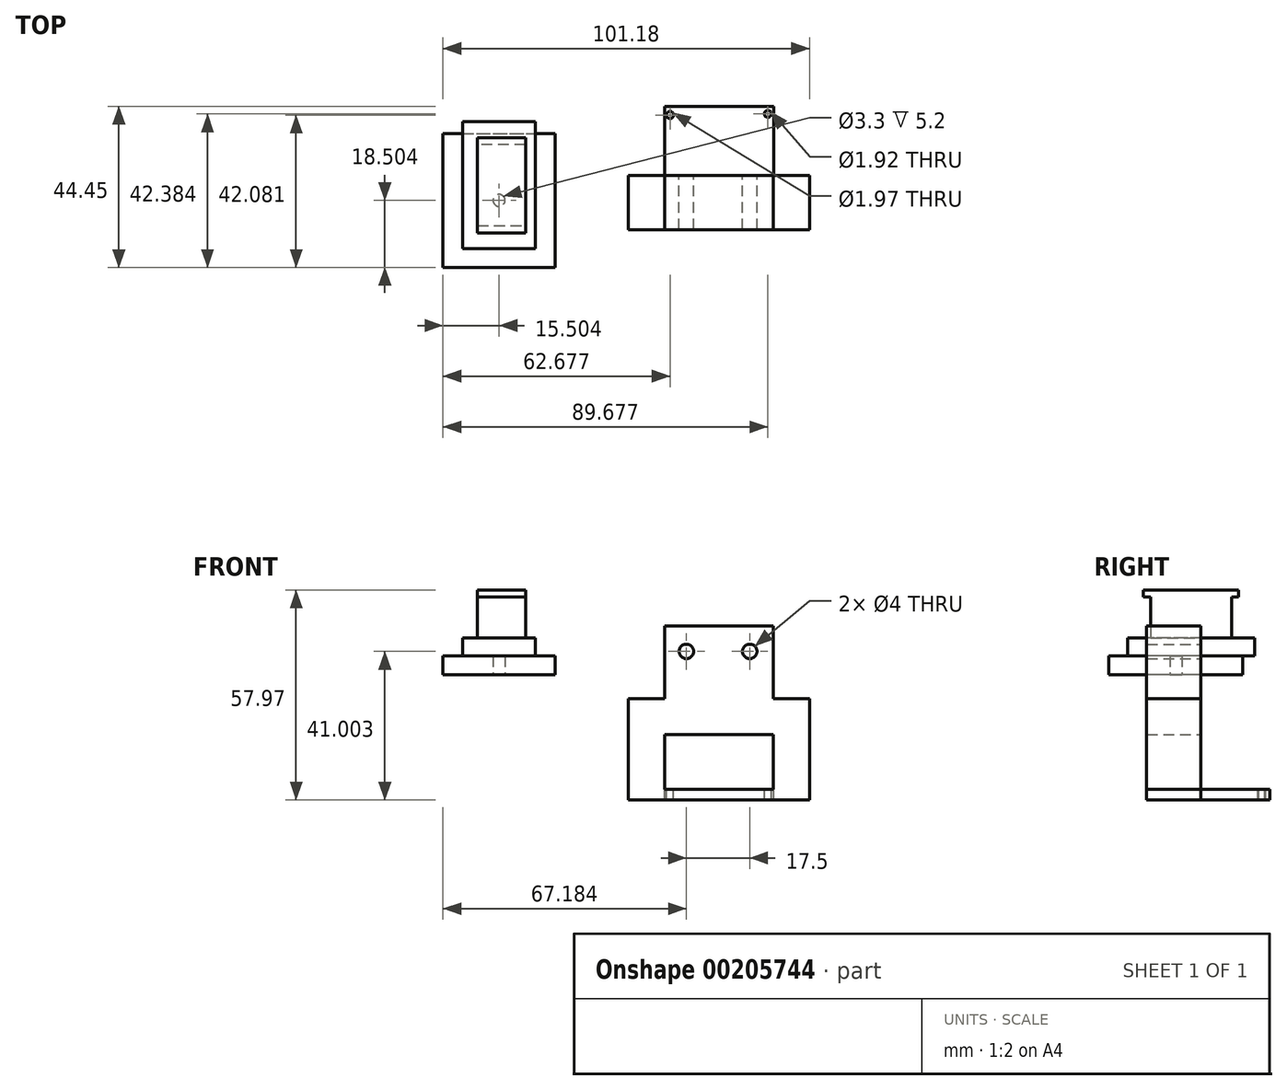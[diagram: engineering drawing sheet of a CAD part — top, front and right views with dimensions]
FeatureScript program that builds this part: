
annotation { "Feature Type Name" : "Feature", "Feature Type Description" : "" }
export const myFeature = defineFeature(function(context is Context, id is Id, definition is map)
    precondition{}
    {
        {
            var Q0;
            Q0=qCreatedBy(makeId("Front.planeOp"),FACE);
            var sketch = newSketch(context, id + "F0", { "sketchPlane" : qUnion([Q0])});
            skLineSegment(sketch, "E0.bottom", {"start": v(-18.33, 11.23) * mm, "end": v(11.67, 11.23) * mm});
            skLineSegment(sketch, "E0.top", {"start": v(-18.33, -18.77) * mm, "end": v(11.67, -18.77) * mm});
            skLineSegment(sketch, "E0.left", {"start": v(-18.33, 11.23) * mm, "end": v(-18.33, -18.77) * mm});
            skLineSegment(sketch, "E0.right", {"start": v(11.67, 11.23) * mm, "end": v(11.67, -18.77) * mm});
            skCircle(sketch, "E1", {"center": v(-12.33, 4.23) * mm, "radius": 2 * mm});
            skCircle(sketch, "E2", {"center": v(5.17, 4.23) * mm, "radius": 2 * mm});
            skPoint(sketch, "E3", {"position": v(-3.33, 11.23) * mm});
            skSolve(sketch);
        }
        {
            var Q0;
            Q0=makeQuery(id+"F0.imprint","IMPRINT",FACE,{"disambiguationData":[TD([[makeQuery(id+"F0.imprint","IMPRINT",EDGE,{"derivedFrom":sQuery(id+"F0.wireOp",EDGE,"E0.bottom")}),-1.0]])]});
            extrude(context, id + "F1", {"entities" : qUnion([Q0]), "depth" : 15 * mm});
        }
        {
            var Q0;
            Q0=makeQuery(id+"F1.opExtrude","SWEPT_FACE",FACE,{"disambiguationData":[OSD([sQuery(id+"F0.wireOp",EDGE,"E0.left")])]});
            var sketch = newSketch(context, id + "F2", { "sketchPlane" : qUnion([Q0])});
            skLineSegment(sketch, "E4.bottom", {"start": v(0, -8.77) * mm, "end": v(15, -8.77) * mm});
            skLineSegment(sketch, "E4.top", {"start": v(0, -33.77) * mm, "end": v(15, -33.77) * mm});
            skLineSegment(sketch, "E4.left", {"start": v(0, -8.77) * mm, "end": v(0, -33.77) * mm});
            skLineSegment(sketch, "E4.right", {"start": v(15, -8.77) * mm, "end": v(15, -33.77) * mm});
            skPoint(sketch, "E5", {"position": v(15, -3.77) * mm});
            skSolve(sketch);
        }
        {
            var Q0;
            Q0 = qSketchRegion(id + "F2", true);
            extrude(context, id + "F3", {"entities" : qUnion([Q0]), "operationType" : NewBodyOperationType.ADD, "depth" : 10 * mm});
        }
        {
            var Q0;
            Q0=makeQuery(id+"F1.opExtrude","SWEPT_FACE",FACE,{"disambiguationData":[OSD([sQuery(id+"F0.wireOp",EDGE,"E0.right")])]});
            var sketch = newSketch(context, id + "F4", { "sketchPlane" : qUnion([Q0])});
            skLineSegment(sketch, "E6.bottom", {"start": v(-15, -8.77) * mm, "end": v(0, -8.77) * mm});
            skLineSegment(sketch, "E6.top", {"start": v(-15, -33.77) * mm, "end": v(0, -33.77) * mm});
            skLineSegment(sketch, "E6.left", {"start": v(-15, -8.77) * mm, "end": v(-15, -33.77) * mm});
            skLineSegment(sketch, "E6.right", {"start": v(0, -8.77) * mm, "end": v(0, -33.77) * mm});
            skSolve(sketch);
        }
        {
            var Q0;
            Q0 = qSketchRegion(id + "F4", true);
            extrude(context, id + "F5", {"entities" : qUnion([Q0]), "operationType" : NewBodyOperationType.ADD, "depth" : 10 * mm});
        }
        {
            var Q0;
            Q0=makeQuery(id+"F3.opExtrude","SWEPT_FACE",FACE,{"disambiguationData":[OSD([sQuery(id+"F2.wireOp",EDGE,"E4.top")])]});
            var sketch = newSketch(context, id + "F6", { "sketchPlane" : qUnion([Q0])});
            skLineSegment(sketch, "E7.bottom", {"start": v(-28.33, 15) * mm, "end": v(21.65, 15) * mm});
            skLineSegment(sketch, "E7.top", {"start": v(-28.33, 0) * mm, "end": v(21.65, 0) * mm});
            skLineSegment(sketch, "E7.left", {"start": v(-28.33, 15) * mm, "end": v(-28.33, 0) * mm});
            skLineSegment(sketch, "E7.right", {"start": v(21.65, 15) * mm, "end": v(21.65, 0) * mm});
            skLineSegment(sketch, "E8.bottom", {"start": v(-18.33, 0) * mm, "end": v(11.76, 0) * mm});
            skLineSegment(sketch, "E8.top", {"start": v(-18.33, -19) * mm, "end": v(11.76, -19) * mm});
            skLineSegment(sketch, "E8.left", {"start": v(-18.33, 0) * mm, "end": v(-18.33, -19) * mm});
            skLineSegment(sketch, "E8.right", {"start": v(11.76, 0) * mm, "end": v(11.76, -19) * mm});
            skCircle(sketch, "E9", {"center": v(-16.83, -16.63) * mm, "radius": 0.99 * mm});
            skCircle(sketch, "E10", {"center": v(10.17, -16.93) * mm, "radius": 0.96 * mm});
            skSolve(sketch);
        }
        {
            var Q0;
            Q0 = qSketchRegion(id + "F6", true);
            extrude(context, id + "F7", {"entities" : qUnion([Q0]), "operationType" : NewBodyOperationType.ADD, "depth" : 3 * mm});
        }
        {
            var Q0;
            Q0=qCreatedBy(makeId("Top.planeOp"),FACE);
            var sketch = newSketch(context, id + "F8", { "sketchPlane" : qUnion([Q0])});
            skLineSegment(sketch, "E11.bottom", {"start": v(-79.5, 11.55) * mm, "end": v(-48.5, 11.55) * mm});
            skLineSegment(sketch, "E11.top", {"start": v(-79.5, -25.45) * mm, "end": v(-48.5, -25.45) * mm});
            skLineSegment(sketch, "E11.left", {"start": v(-79.5, 11.55) * mm, "end": v(-79.5, -25.45) * mm});
            skLineSegment(sketch, "E11.right", {"start": v(-48.5, 11.55) * mm, "end": v(-48.5, -25.45) * mm});
            skLineSegment(sketch, "E12", {"start": v(-64, 11.55) * mm, "end": v(-64, -25.45) * mm, "construction": true});
            skLineSegment(sketch, "E13", {"start": v(-79.5, -6.95) * mm, "end": v(-48.5, -6.95) * mm, "construction": true});
            skCircle(sketch, "E14", {"center": v(-64, -6.95) * mm, "radius": 1.65 * mm});
            skSolve(sketch);
        }
        {
            var Q0;
            Q0 = qSketchRegion(id + "F8", true);
            extrude(context, id + "F9", {"entities" : qUnion([Q0]), "depth" : 3 * mm});
        }
        {
            var Q0;
            Q0=makeQuery(id+"F9.opExtrude","CAP_FACE",FACE,{"disambiguationData":[OSD([sQuery(id+"F8.wireOp",EDGE,"E11.bottom"),sQuery(id+"F8.wireOp",EDGE,"E11.top"),sQuery(id+"F8.wireOp",EDGE,"E11.left"),sQuery(id+"F8.wireOp",EDGE,"E11.right"),sQuery(id+"F8.wireOp",EDGE,"IWCKZ5gG-MOeN-IYZW-2EvN-JKWWDjgxmHPc"),sQuery(id+"F8.wireOp",EDGE,"644afa14-c5a4-4717-896c-2b00ea7ac0db0.MirrorC"),sQuery(id+"F8.wireOp",EDGE,"57038aa0-a765-417c-a0be-fbad03bbe3f50.MirrorC"),sQuery(id+"F8.wireOp",EDGE,"708bdf5b-5082-4a79-8eaa-554b4d0072140.MirrorC")])],"isStart":false});
            var sketch = newSketch(context, id + "F10", { "sketchPlane" : qUnion([Q0])});
            skLineSegment(sketch, "E15.bottom", {"start": v(-74, 14.75) * mm, "end": v(-54, 14.75) * mm});
            skLineSegment(sketch, "E15.top", {"start": v(-74, -20.25) * mm, "end": v(-54, -20.25) * mm});
            skLineSegment(sketch, "E15.left", {"start": v(-74, 14.75) * mm, "end": v(-74, -20.25) * mm});
            skLineSegment(sketch, "E15.right", {"start": v(-54, 14.75) * mm, "end": v(-54, -20.25) * mm});
            skLineSegment(sketch, "E16.bottom", {"start": v(-70.01, 8.4) * mm, "end": v(-56.71, 8.4) * mm});
            skLineSegment(sketch, "E16.top", {"start": v(-70.01, -13.9) * mm, "end": v(-56.71, -13.9) * mm});
            skLineSegment(sketch, "E16.left", {"start": v(-70.01, 8.4) * mm, "end": v(-70.01, -13.9) * mm});
            skLineSegment(sketch, "E16.right", {"start": v(-56.71, 8.4) * mm, "end": v(-56.71, -13.9) * mm});
            skPoint(sketch, "E16.middle", {"position": v(-63.36, -2.75) * mm});
            skPoint(sketch, "E16.middle.positionSnap0", {"position": v(-54, -2.75) * mm});
            skPoint(sketch, "E16.centerSnap0", {"position": v(-54, -2.75) * mm});
            skPoint(sketch, "E17", {"position": v(-64, 14.75) * mm});
            skSolve(sketch);
        }
        {
            var Q0;
            Q0 = qSketchRegion(id + "F10", true);
            var Q1;
            Q1=makeQuery(id+"F10.imprint","IMPRINT",FACE,{"disambiguationData":[TD([[makeQuery(id+"F10.imprint","IMPRINT",EDGE,{"derivedFrom":sQuery(id+"F10.wireOp",EDGE,"E16.bottom")}),-1.0]])]});
            var Q2;
            Q2=makeQuery(id+"F10.imprint","IMPRINT",FACE,{"disambiguationData":[TD([[makeQuery(id+"F10.imprint","IMPRINT",EDGE,{"derivedFrom":makeQuery(id+"F9.opExtrude","CAP_EDGE",EDGE,{"disambiguationData":[OSD([sQuery(id+"F8.wireOp",EDGE,"E14")])],"isStart":false})}),1.0]])]});
            extrude(context, id + "F11", {"entities" : qUnion([Q0, Q1, Q2]), "operationType" : NewBodyOperationType.ADD, "depth" : 5 * mm});
        }
        {
            var Q0;
            Q0=makeQuery(id+"F10.imprint","IMPRINT",FACE,{"disambiguationData":[TD([[makeQuery(id+"F10.imprint","IMPRINT",EDGE,{"derivedFrom":sQuery(id+"F10.wireOp",EDGE,"E16.bottom")}),-1.0]])]});
            var Q1;
            Q1=makeQuery(id+"F10.imprint","IMPRINT",FACE,{"disambiguationData":[TD([[makeQuery(id+"F10.imprint","IMPRINT",EDGE,{"derivedFrom":makeQuery(id+"F9.opExtrude","CAP_EDGE",EDGE,{"disambiguationData":[OSD([sQuery(id+"F8.wireOp",EDGE,"E14")])],"isStart":false})}),1.0]])]});
            extrude(context, id + "F12", {"entities" : qUnion([Q0, Q1]), "operationType" : NewBodyOperationType.ADD, "depth" : 18.2 * mm});
        }
        {
            var Q0;
            Q0=makeQuery(id+"F12.opExtrude","SWEPT_FACE",FACE,{"disambiguationData":[OSD([sQuery(id+"F10.wireOp",EDGE,"E16.top")])]});
            var sketch = newSketch(context, id + "F13", { "sketchPlane" : qUnion([Q0])});
            skLineSegment(sketch, "E18.bottom", {"start": v(-70.01, 21.2) * mm, "end": v(-56.71, 21.2) * mm});
            skLineSegment(sketch, "E18.top", {"start": v(-70.01, 19.2) * mm, "end": v(-56.71, 19.2) * mm});
            skLineSegment(sketch, "E18.left", {"start": v(-70.01, 21.2) * mm, "end": v(-70.01, 19.2) * mm});
            skLineSegment(sketch, "E18.right", {"start": v(-56.71, 21.2) * mm, "end": v(-56.71, 19.2) * mm});
            skPoint(sketch, "E18.middle", {"position": v(-63.36, 20.2) * mm});
            skPoint(sketch, "E18.middle.positionSnap0", {"position": v(-63.36, 21.2) * mm});
            skPoint(sketch, "E18.centerSnap0", {"position": v(-63.36, 21.2) * mm});
            skSolve(sketch);
        }
        {
            var Q0;
            Q0 = qSketchRegion(id + "F13", true);
            extrude(context, id + "F14", {"entities" : qUnion([Q0]), "operationType" : NewBodyOperationType.ADD, "depth" : 2 * mm});
        }
        {
            var Q0;
            Q0=makeQuery(id+"F12.opExtrude","SWEPT_FACE",FACE,{"disambiguationData":[OSD([sQuery(id+"F10.wireOp",EDGE,"E16.bottom")])]});
            var sketch = newSketch(context, id + "F15", { "sketchPlane" : qUnion([Q0])});
            skLineSegment(sketch, "E19.bottom", {"start": v(56.71, 21.2) * mm, "end": v(70.01, 21.2) * mm});
            skLineSegment(sketch, "E19.top", {"start": v(56.71, 19.2) * mm, "end": v(70.01, 19.2) * mm});
            skLineSegment(sketch, "E19.left", {"start": v(56.71, 21.2) * mm, "end": v(56.71, 19.2) * mm});
            skLineSegment(sketch, "E19.right", {"start": v(70.01, 21.2) * mm, "end": v(70.01, 19.2) * mm});
            skPoint(sketch, "E19.middle", {"position": v(63.36, 20.2) * mm});
            skPoint(sketch, "E19.middle.positionSnap0", {"position": v(63.36, 21.2) * mm});
            skPoint(sketch, "E19.centerSnap0", {"position": v(63.36, 21.2) * mm});
            skSolve(sketch);
        }
        {
            var Q0;
            Q0 = qSketchRegion(id + "F15", true);
            extrude(context, id + "F16", {"entities" : qUnion([Q0]), "operationType" : NewBodyOperationType.ADD, "depth" : 2 * mm});
        }
        {
            var Q0;
            Q0=makeQuery(id+"F9.opExtrude","CAP_FACE",FACE,{"disambiguationData":[OSD([sQuery(id+"F8.wireOp",EDGE,"E11.bottom"),sQuery(id+"F8.wireOp",EDGE,"E11.top"),sQuery(id+"F8.wireOp",EDGE,"E11.left"),sQuery(id+"F8.wireOp",EDGE,"E11.right"),sQuery(id+"F8.wireOp",EDGE,"E14")])],"isStart":true});
            extrude(context, id + "F17", {"entities" : qUnion([Q0]), "operationType" : NewBodyOperationType.ADD, "depth" : 2.2 * mm});
        }
    });
